# Revit family: Haworth_Belong_Blotter
name_source: partatom
category: Furniture Systems
revit_build: Autodesk Revit 2018 (Build: 20170223_1515(x64)
units: mm (PartAtom-declared; Revit-internal decimal feet)

## family parameters
Always vertical = Yes
Cut with Voids When Loaded = No
OmniClass Number = 23.25.40.00
OmniClass Title = Space Division Products
Part Type = Normal
Room Calculation Point = No
Round Connector Dimension = Use Diameter
Shared = No
Work Plane-Based = No

## types (1)
- Blotter
    Actual Depth = 2' - 0"
    Actual Width = 3' - 0"
    Assembly Code = E2020200
    Blotter Finish = Haworth _ Polymer _ Fog
    Custom 20 = Yes
    Custom 24 = No
    Custom Size = No
    Depth = 2' - 0"
    Description = Haworth_Belong-Blotter
    Manufacturer = Haworth
    Max. Depth = 2' - 0"
    Max. Width = 5' - 0"
    Min. Depth = 1' - 8"
    Min. Width = 2' - 0"
    Model = Haworth - Belong - Blotter
    Revision = 2
    Size = Verify Final Dimensions With Haworth
    Standard Sizes = 36w x 24d, 36w x 20d, 30w x 20d
    Sustainability Info = https://www.haworth.com
    URL = www.haworth.com
    URL - Product = http://www.haworth.com
    Warranty = http://www.haworth.com
    Width = 3' - 0"

## geometry (parser evidence)
native form markers: Sweep x3
no freeform markers — native parametric forms only
